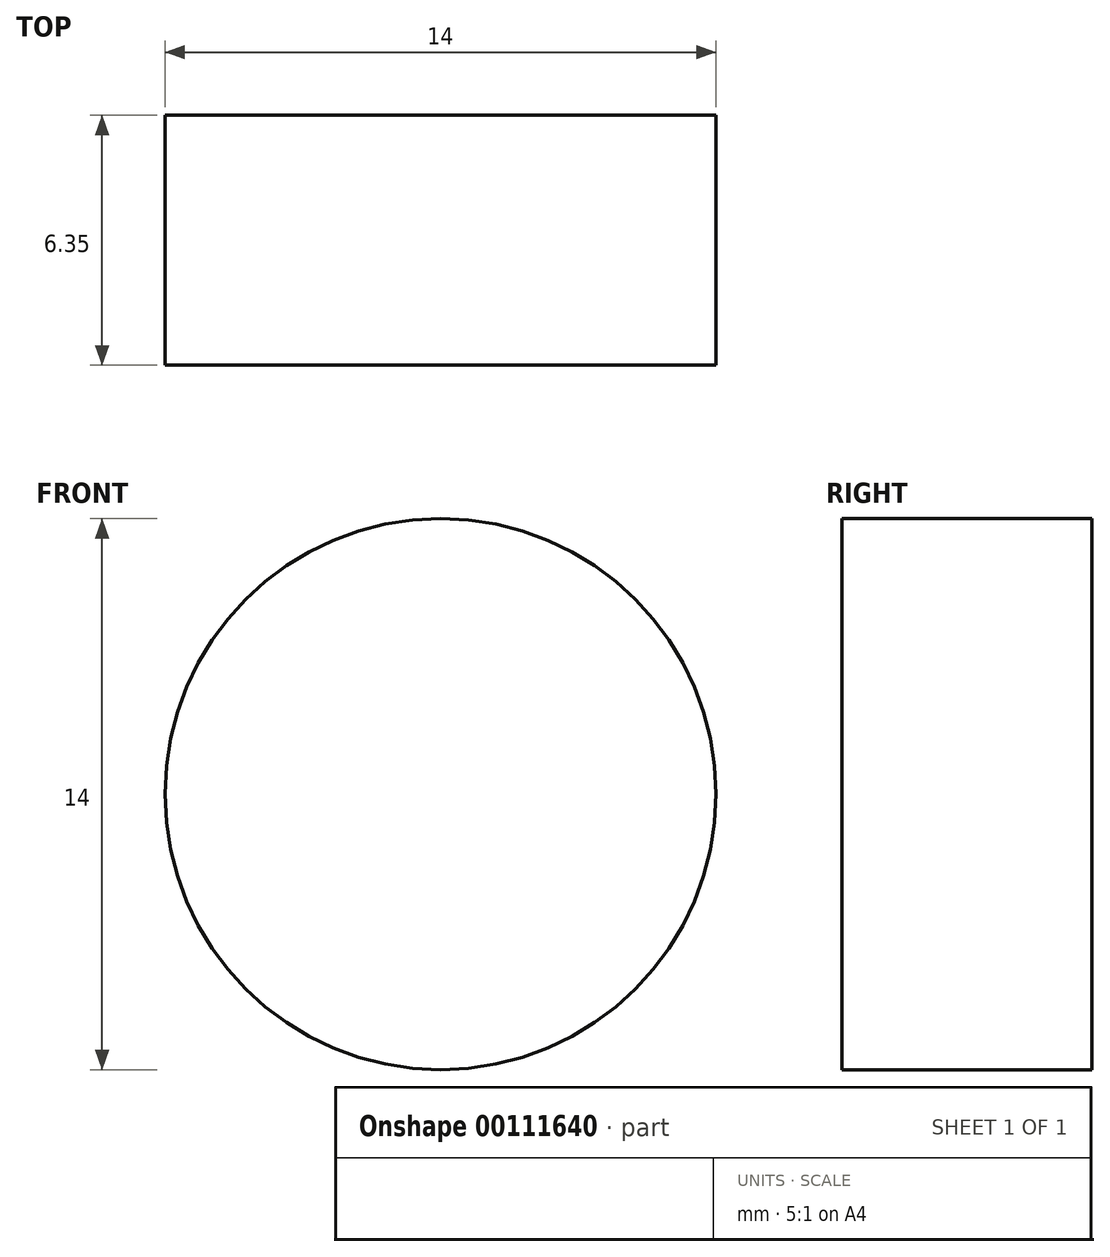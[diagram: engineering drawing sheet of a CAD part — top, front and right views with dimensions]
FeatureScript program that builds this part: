
annotation { "Feature Type Name" : "Feature", "Feature Type Description" : "" }
export const myFeature = defineFeature(function(context is Context, id is Id, definition is map)
    precondition{}
    {
        {
            var Q0;
            Q0=qCreatedBy(makeId("Front.planeOp"),FACE);
            var sketch = newSketch(context, id + "F0", { "sketchPlane" : qUnion([Q0])});
            skCircle(sketch, "E0", {"center": v(0, 0) * mm, "radius": 7 * mm});
            skLineSegment(sketch, "E1", {"start": v(-7, 0) * mm, "end": v(7, 0) * mm});
            skSolve(sketch);
        }
        {
            var Q0;
            Q0 = qSketchRegion(id + "F0", true);
            extrude(context, id + "F1", {"entities" : qUnion([Q0]), "depth" : 6.35 * mm});
        }
    });
